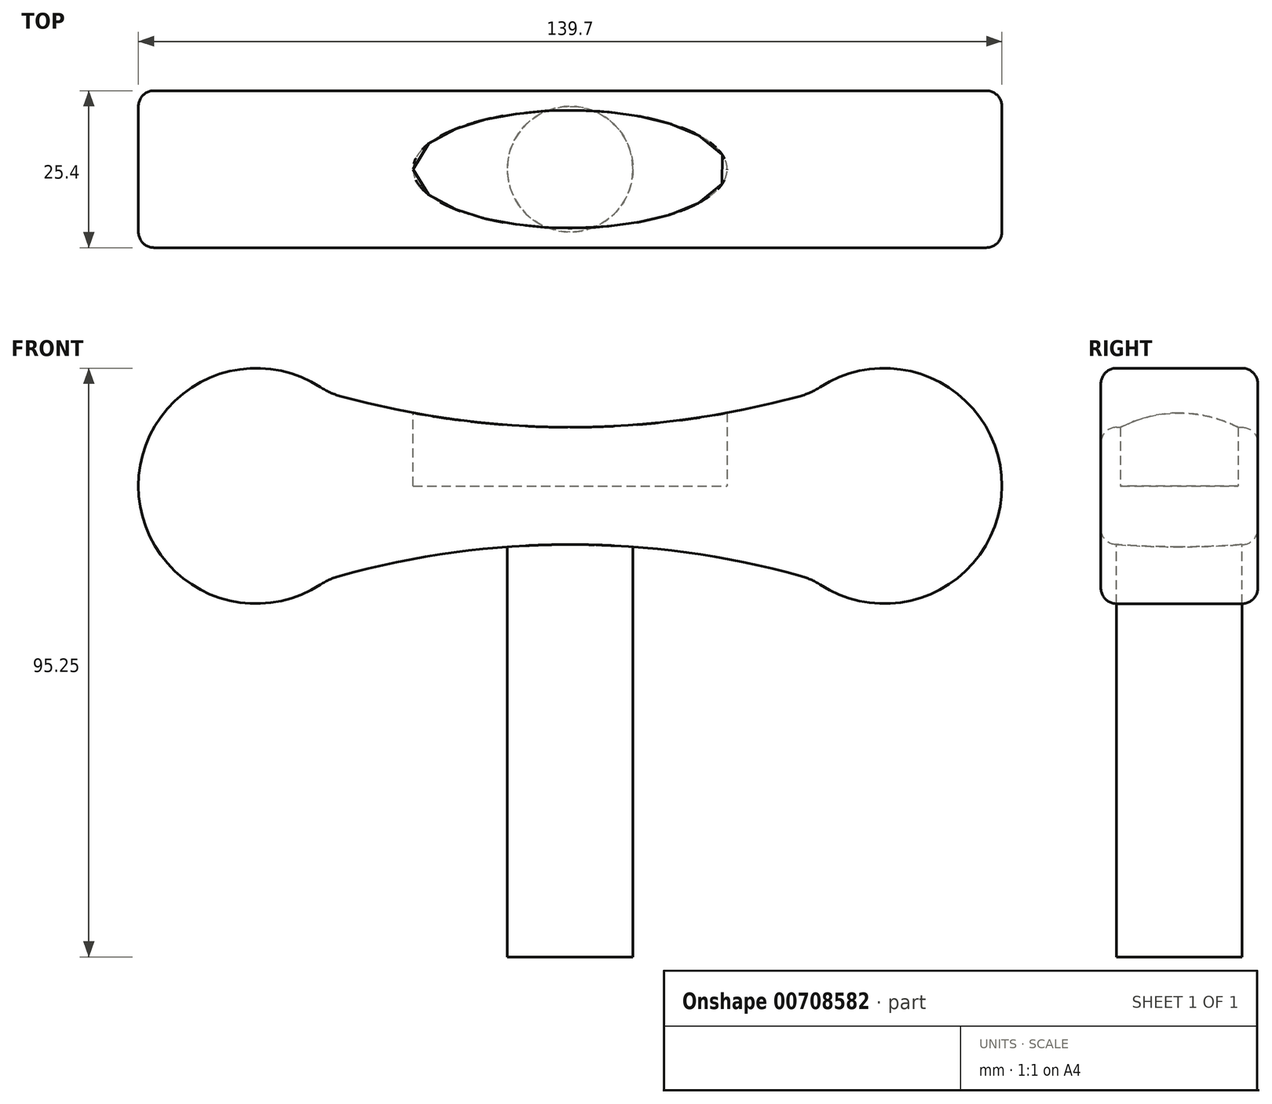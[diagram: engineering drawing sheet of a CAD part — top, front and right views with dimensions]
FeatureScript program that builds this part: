
annotation { "Feature Type Name" : "Feature", "Feature Type Description" : "" }
export const myFeature = defineFeature(function(context is Context, id is Id, definition is map)
    precondition{}
    {
        {
            var Q0;
            Q0=qCreatedBy(makeId("Front.planeOp"),FACE);
            var sketch = newSketch(context, id + "F0", { "sketchPlane" : qUnion([Q0])});
            skLineSegment(sketch, "E0", {"start": v(0, 0) * mm, "end": v(-50.8, 0) * mm});
            skLineSegment(sketch, "E1", {"start": v(0, 0) * mm, "end": v(50.8, 0) * mm});
            skArc(sketch, "E2", {"start": v(-40.42, 15.97) * mm, "mid": v(-69.85, 0) * mm, "end": v(-40.42, -15.97) * mm});
            skArc(sketch, "E3", {"start": v(40.42, -15.97) * mm, "mid": v(69.85, 0) * mm, "end": v(40.42, 15.97) * mm});
            skArc(sketch, "E4", {"start": v(-37.24, 14.54) * mm, "mid": v(0, 9.49) * mm, "end": v(37.24, 14.54) * mm});
            skArc(sketch, "E5", {"start": v(37.24, -14.54) * mm, "mid": v(0, -9.49) * mm, "end": v(-37.24, -14.54) * mm});
            skPoint(sketch, "E6.orphan", {"position": v(50.8, -19.05) * mm});
            skPoint(sketch, "E7.orphan", {"position": v(-50.8, -19.05) * mm});
            skPoint(sketch, "E8.orphan", {"position": v(-50.8, 19.05) * mm});
            skPoint(sketch, "E9.visualSharp", {"position": v(-39.17, 15.1) * mm});
            skArc(sketch, "E9.filletArc", {"start": v(-40.42, 15.97) * mm, "mid": v(-38.88, 15.13) * mm, "end": v(-37.24, 14.54) * mm});
            skPoint(sketch, "E10.visualSharp", {"position": v(-39.17, -15.1) * mm});
            skArc(sketch, "E10.filletArc", {"start": v(-37.24, -14.54) * mm, "mid": v(-38.88, -15.13) * mm, "end": v(-40.42, -15.97) * mm});
            skPoint(sketch, "E11.visualSharp", {"position": v(50.8, 19.05) * mm});
            skArc(sketch, "E11.filletArc", {"start": v(37.24, 14.54) * mm, "mid": v(38.88, 15.13) * mm, "end": v(40.42, 15.97) * mm});
            skArc(sketch, "E12.filletArc", {"start": v(40.42, -15.97) * mm, "mid": v(38.88, -15.13) * mm, "end": v(37.24, -14.54) * mm});
            skSolve(sketch);
        }
        {
            var Q0;
            Q0 = qSketchRegion(id + "F0", true);
            extrude(context, id + "F1", {"entities" : qUnion([Q0]), "endBound" : BoundingType.SYMMETRIC, "depth" : 25.4 * mm, "offsetDistance" : 25.4 * mm});
        }
        {
            var Q0;
            Q0=makeQuery(id+"F1.opExtrude","CAP_EDGE",EDGE,{"disambiguationData":[OSD([sQuery(id+"F0.wireOp",EDGE,"E2")])],"isStart":false});
            var Q1;
            Q1=makeQuery(id+"F1.opExtrude","CAP_EDGE",EDGE,{"disambiguationData":[OSD([sQuery(id+"F0.wireOp",EDGE,"E2")])],"isStart":true});
            fillet(context, id + "F2", {"entities" : qUnion([Q0, Q1]), "radius" : 2.54 * mm, "tangentPropagation" : true, "allowEdgeOverflow" : false});
        }
        {
            var Q0;
            Q0=qCreatedBy(makeId("Top.planeOp"),FACE);
            var sketch = newSketch(context, id + "F3", { "sketchPlane" : qUnion([Q0])});
            skCircle(sketch, "E13", {"center": v(0, 0) * mm, "radius": 10.16 * mm});
            skSolve(sketch);
        }
        {
            var Q0;
            Q0 = qSketchRegion(id + "F3", true);
            extrude(context, id + "F4", {"entities" : qUnion([Q0]), "operationType" : NewBodyOperationType.ADD, "oppositeDirection" : true, "depth" : 76.2 * mm, "offsetDistance" : 25.4 * mm});
        }
        {
            var Q0;
            Q0=qCreatedBy(makeId("Top.planeOp"),FACE);
            cPlane(context, id + "F5", {"entities" : qUnion([Q0]), "cplaneType" : CPlaneType.OFFSET, "offset" : 19.05 * mm, "width" : 152.4 * mm, "height" : 152.4 * mm});
        }
        {
            var Q0;
            Q0=qCreatedBy(id+"F5.planeOp",FACE);
            var sketch = newSketch(context, id + "F6", { "sketchPlane" : qUnion([Q0])});
            skEllipse(sketch, "E14", {"center": v(0, 0) * mm, "majorRadius": 25.4 * mm, "minorRadius": 9.53 * mm, "majorAxis": v(-1, 0)});
            skSolve(sketch);
        }
        {
            var Q0;
            Q0 = qSketchRegion(id + "F6", true);
            extrude(context, id + "F7", {"entities" : qUnion([Q0]), "operationType" : NewBodyOperationType.REMOVE, "oppositeDirection" : true, "depth" : 19.05 * mm, "offsetDistance" : 25.4 * mm});
        }
    });
